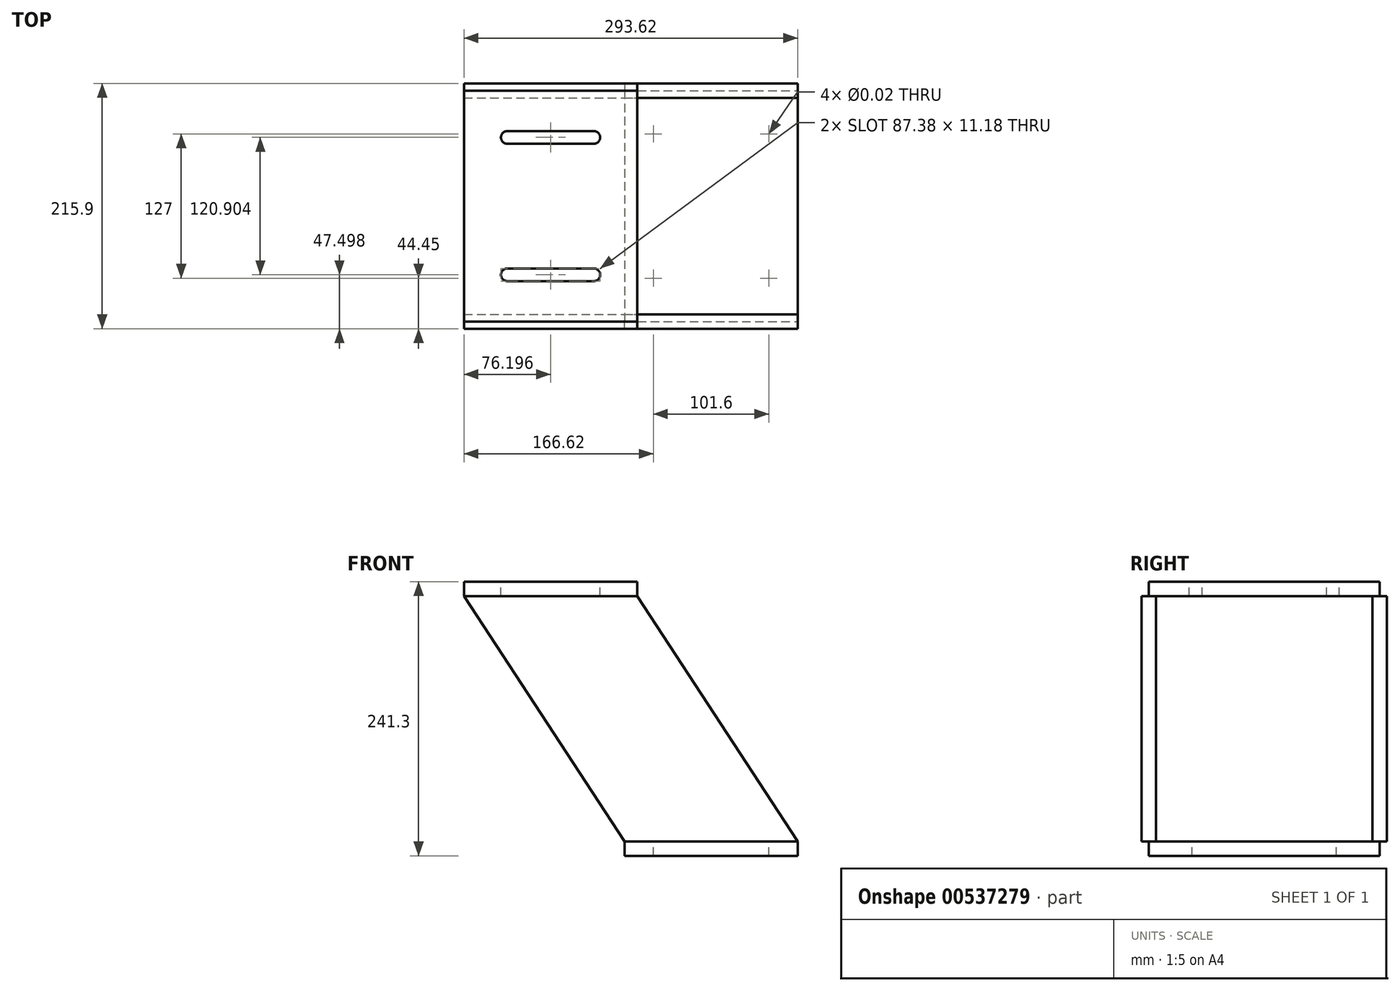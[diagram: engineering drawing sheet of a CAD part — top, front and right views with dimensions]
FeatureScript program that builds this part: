
annotation { "Feature Type Name" : "Feature", "Feature Type Description" : "" }
export const myFeature = defineFeature(function(context is Context, id is Id, definition is map)
    precondition{}
    {
        {
            var Q0;
            Q0=qCreatedBy(makeId("Top.planeOp"),FACE);
            var sketch = newSketch(context, id + "F0", { "sketchPlane" : qUnion([Q0])});
            skLineSegment(sketch, "E0.bottom", {"start": v(-76.2, 101.6) * mm, "end": v(76.2, 101.6) * mm});
            skLineSegment(sketch, "E0.top", {"start": v(-76.2, -101.6) * mm, "end": v(76.2, -101.6) * mm});
            skLineSegment(sketch, "E0.left", {"start": v(-76.2, 101.6) * mm, "end": v(-76.2, -101.6) * mm});
            skLineSegment(sketch, "E0.right", {"start": v(76.2, 101.6) * mm, "end": v(76.2, -101.6) * mm});
            skPoint(sketch, "E0.middle", {"position": v(0, 0) * mm});
            skSolve(sketch);
        }
        {
            var Q0;
            Q0 = qSketchRegion(id + "F0", true);
            extrude(context, id + "F1", {"entities" : qUnion([Q0]), "depth" : 12.7 * mm, "offsetDistance" : 25.4 * mm});
        }
        {
            var Q0;
            Q0=makeQuery(id+"F1.opExtrude","CAP_FACE",FACE,{"disambiguationData":[OSD([sQuery(id+"F0.wireOp",EDGE,"E0.bottom"),sQuery(id+"F0.wireOp",EDGE,"E0.top"),sQuery(id+"F0.wireOp",EDGE,"E0.left"),sQuery(id+"F0.wireOp",EDGE,"E0.right")])],"isStart":false});
            var sketch = newSketch(context, id + "F2", { "sketchPlane" : qUnion([Q0])});
            skLineSegment(sketch, "E1", {"start": v(0, 155.9) * mm, "end": v(0, -175.28) * mm, "construction": true});
            skPoint(sketch, "E1.endSnap0", {"position": v(0, 101.6) * mm});
            skLineSegment(sketch, "E2", {"start": v(-174.3, 0) * mm, "end": v(170.43, 0) * mm, "construction": true});
            skPoint(sketch, "E2.endSnap0", {"position": v(76.2, 0) * mm});
            skLineSegment(sketch, "E3.0", {"start": v(-50.8, 155.9) * mm, "end": v(-50.8, -175.28) * mm, "construction": true});
            skLineSegment(sketch, "E4.0", {"start": v(-174.3, 63.5) * mm, "end": v(170.43, 63.5) * mm, "construction": true});
            skPoint(sketch, "E5", {"position": v(-50.8, 63.5) * mm});
            skPoint(sketch, "E6.MirrorP", {"position": v(-50.8, -63.5) * mm});
            skPoint(sketch, "E7.MirrorP", {"position": v(50.8, 63.5) * mm});
            skPoint(sketch, "E8.MirrorP", {"position": v(50.8, -63.5) * mm});
            skSolve(sketch);
        }
        {
            var Q0;
            Q0=sQuery(id+"F2.wireOp",VERTEX,"E5");
            var Q1;
            Q1=sQuery(id+"F2.wireOp",VERTEX,"E7.MirrorP");
            var Q2;
            Q2=sQuery(id+"F2.wireOp",VERTEX,"E6.MirrorP");
            var Q3;
            Q3=sQuery(id+"F2.wireOp",VERTEX,"E8.MirrorP");
            var Q4;
            Q4=makeQuery(id+"F1.opExtrude","SWEPT_BODY",BODY,{"disambiguationData":[OSD([sQuery(id+"F0.wireOp",EDGE,"E0.bottom"),sQuery(id+"F0.wireOp",EDGE,"E0.top"),sQuery(id+"F0.wireOp",EDGE,"E0.left"),sQuery(id+"F0.wireOp",EDGE,"E0.right")])]});
            hole(context, id + "F3", {"style" : HoleStyle.SIMPLE, "endStyle" : HoleEndStyle.THROUGH, "standardTappedOrClearance" : lookupTablePath({ "standard" : "ANSI", "size" : "9/16 (0.56)", "type" : "Drilled" }), "standardBlindInLast" : lookupTablePath({ "standard" : "ANSI", "size" : "9/16", "type" : "Drilled" }), "holeDiameter" : 9 / 406.4 * mm, "isTappedThrough" : true, "tappedDepth" : 12.06 * mm, "tapClearance" : 3, "startFromSketch" : true, "locations" : qUnion([Q0, Q1, Q2, Q3]), "scope" : qUnion([Q4])});
        }
        {
            var Q0;
            Q0=makeQuery(id+"F1.opExtrude","CAP_FACE",FACE,{"disambiguationData":[OSD([sQuery(id+"F0.wireOp",EDGE,"E0.bottom"),sQuery(id+"F0.wireOp",EDGE,"E0.top"),sQuery(id+"F0.wireOp",EDGE,"E0.left"),sQuery(id+"F0.wireOp",EDGE,"E0.right")])],"isStart":true});
            cPlane(context, id + "F4", {"entities" : qUnion([Q0]), "cplaneType" : CPlaneType.OFFSET, "offset" : 241.3 * mm, "oppositeDirection" : true, "width" : 152.4 * mm, "height" : 152.4 * mm});
        }
        {
            var Q0;
            Q0=qCreatedBy(id+"F4.planeOp",FACE);
            var sketch = newSketch(context, id + "F5", { "sketchPlane" : qUnion([Q0])});
            skLineSegment(sketch, "E9.0", {"start": v(0, -155.9) * mm, "end": v(0, 175.28) * mm, "construction": true});
            skLineSegment(sketch, "E10.0", {"start": v(-174.3, 0) * mm, "end": v(170.43, 0) * mm, "construction": true});
            skLineSegment(sketch, "E11.0", {"start": v(-141.22, -155.9) * mm, "end": v(-141.22, 175.28) * mm, "construction": true});
            skLineSegment(sketch, "E12.bottom", {"start": v(-217.42, 101.6) * mm, "end": v(-65.02, 101.6) * mm});
            skLineSegment(sketch, "E12.top", {"start": v(-217.42, -101.6) * mm, "end": v(-65.02, -101.6) * mm});
            skLineSegment(sketch, "E12.left", {"start": v(-217.42, 101.6) * mm, "end": v(-217.42, -101.6) * mm});
            skLineSegment(sketch, "E12.right", {"start": v(-65.02, 101.6) * mm, "end": v(-65.02, -101.6) * mm});
            skPoint(sketch, "E12.middle", {"position": v(-141.22, 0) * mm});
            skSolve(sketch);
        }
        {
            var Q0;
            Q0=makeQuery(id+"F5.imprint","IMPRINT",FACE,{"disambiguationData":[TD([[makeQuery(id+"F5.imprint","IMPRINT",EDGE,{"derivedFrom":sQuery(id+"F5.wireOp",EDGE,"E12.bottom")}),-1.0]])]});
            extrude(context, id + "F6", {"entities" : qUnion([Q0]), "depth" : 12.7 * mm, "offsetDistance" : 25.4 * mm});
        }
        {
            var Q0;
            Q0=makeQuery(id+"F6.opExtrude","CAP_FACE",FACE,{"disambiguationData":[OSD([sQuery(id+"F5.wireOp",EDGE,"E12.bottom"),sQuery(id+"F5.wireOp",EDGE,"E12.top"),sQuery(id+"F5.wireOp",EDGE,"E12.left"),sQuery(id+"F5.wireOp",EDGE,"E12.right")])],"isStart":true});
            var sketch = newSketch(context, id + "F7", { "sketchPlane" : qUnion([Q0])});
            skLineSegment(sketch, "E13", {"start": v(-141.22, 101.6) * mm, "end": v(-141.22, -127.83) * mm, "construction": true});
            skLineSegment(sketch, "E14", {"start": v(-288.63, 0) * mm, "end": v(116.16, 0) * mm, "construction": true});
            skLineSegment(sketch, "E15.0", {"start": v(-179.32, 101.6) * mm, "end": v(-179.32, -127.83) * mm, "construction": true});
            skLineSegment(sketch, "E16.0", {"start": v(-179.32, -60.45) * mm, "end": v(-103.12, -60.45) * mm});
            skLineSegment(sketch, "E17.MirrorCS", {"start": v(-103.12, 101.6) * mm, "end": v(-103.12, -127.83) * mm, "construction": true});
            skArc(sketch, "E18.0.startCap", {"start": v(-179.32, -66.04) * mm, "mid": v(-184.91, -60.45) * mm, "end": v(-179.32, -54.86) * mm});
            skArc(sketch, "E18.0.endCap", {"start": v(-103.12, -54.86) * mm, "mid": v(-97.54, -60.45) * mm, "end": v(-103.12, -66.04) * mm});
            skLineSegment(sketch, "E18.0.left", {"start": v(-179.32, -54.86) * mm, "end": v(-103.12, -54.86) * mm});
            skLineSegment(sketch, "E18.0.right", {"start": v(-179.32, -66.04) * mm, "end": v(-103.12, -66.04) * mm});
            skArc(sketch, "E19.MirrorCS", {"start": v(-103.12, 54.86) * mm, "mid": v(-97.54, 60.45) * mm, "end": v(-103.12, 66.04) * mm});
            skLineSegment(sketch, "E20.MirrorCS", {"start": v(-179.32, 66.04) * mm, "end": v(-103.12, 66.04) * mm});
            skLineSegment(sketch, "E21.MirrorCS", {"start": v(-179.32, 54.86) * mm, "end": v(-103.12, 54.86) * mm});
            skArc(sketch, "E22.MirrorCS", {"start": v(-179.32, 66.04) * mm, "mid": v(-184.91, 60.45) * mm, "end": v(-179.32, 54.86) * mm});
            skLineSegment(sketch, "E23.MirrorCS", {"start": v(-179.32, 60.45) * mm, "end": v(-103.12, 60.45) * mm});
            skSolve(sketch);
        }
        {
            var Q0;
            Q0 = qSketchRegion(id + "F7", true);
            extrude(context, id + "F8", {"entities" : qUnion([Q0]), "operationType" : NewBodyOperationType.REMOVE, "endBound" : BoundingType.THROUGH_ALL, "oppositeDirection" : true, "depth" : 25.4 * mm, "offsetDistance" : 25.4 * mm});
        }
        {
            var Q0;
            Q0=makeQuery(id+"F6.opExtrude","SWEPT_FACE",FACE,{"disambiguationData":[OSD([sQuery(id+"F5.wireOp",EDGE,"E12.bottom")])]});
            var sketch = newSketch(context, id + "F9", { "sketchPlane" : qUnion([Q0])});
            skLineSegment(sketch, "E24.0", {"start": v(-217.42, 228.6) * mm, "end": v(-65.02, 228.6) * mm});
            skLineSegment(sketch, "E25.0", {"start": v(-76.2, 12.7) * mm, "end": v(76.2, 12.7) * mm});
            skLineSegment(sketch, "E26", {"start": v(-217.42, 228.6) * mm, "end": v(-76.2, 12.7) * mm});
            skLineSegment(sketch, "E27", {"start": v(-65.02, 228.6) * mm, "end": v(76.2, 12.7) * mm});
            skSolve(sketch);
        }
        {
            var Q0;
            Q0 = qSketchRegion(id + "F9", true);
            extrude(context, id + "F10", {"entities" : qUnion([Q0]), "endBound" : BoundingType.SYMMETRIC, "depth" : 12.7 * mm, "offsetDistance" : 25.4 * mm});
        }
        {
            var Q0;
            Q0=makeQuery(id+"F10.opExtrude","SWEPT_BODY",BODY,{"disambiguationData":[OSD([sQuery(id+"F9.wireOp",EDGE,"E24.0"),sQuery(id+"F9.wireOp",EDGE,"E25.0"),sQuery(id+"F9.wireOp",EDGE,"E26"),sQuery(id+"F9.wireOp",EDGE,"E27")])]});
            var Q1;
            Q1=qCreatedBy(makeId("Front.planeOp"),FACE);
            mirror(context, id + "F11", {"entities" : qUnion([Q0]), "mirrorPlane" : qUnion([Q1])});
        }
    });
